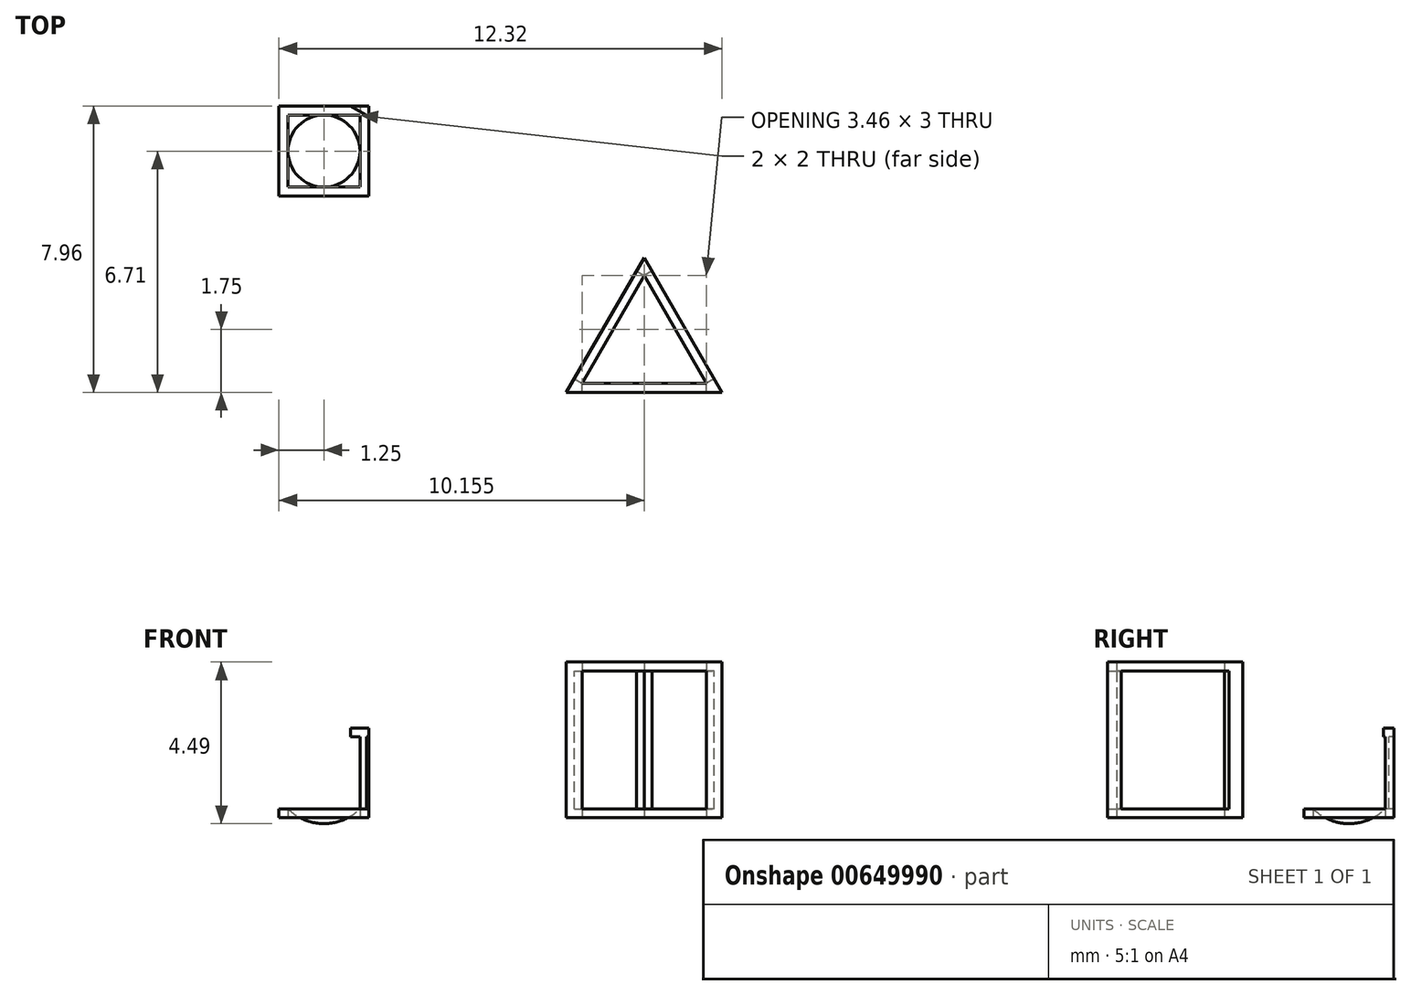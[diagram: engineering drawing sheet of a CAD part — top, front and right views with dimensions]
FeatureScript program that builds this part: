
annotation { "Feature Type Name" : "Feature", "Feature Type Description" : "" }
export const myFeature = defineFeature(function(context is Context, id is Id, definition is map)
    precondition{}
    {
        {
            var Q0;
            Q0=qCreatedBy(makeId("Top.planeOp"),FACE);
            var sketch = newSketch(context, id + "F0", { "sketchPlane" : qUnion([Q0])});
            skLineSegment(sketch, "E0.bottom", {"start": v(1, -1) * mm, "end": v(-1, -1) * mm});
            skLineSegment(sketch, "E0.top", {"start": v(1, 1) * mm, "end": v(-1, 1) * mm});
            skLineSegment(sketch, "E0.left", {"start": v(1, -1) * mm, "end": v(1, 1) * mm});
            skLineSegment(sketch, "E0.right", {"start": v(-1, -1) * mm, "end": v(-1, 1) * mm});
            skPoint(sketch, "E0.middle", {"position": v(0, 0) * mm});
            skLineSegment(sketch, "E1.bottom", {"start": v(1.25, -1.25) * mm, "end": v(-1.25, -1.25) * mm});
            skLineSegment(sketch, "E1.top", {"start": v(1.25, 1.25) * mm, "end": v(-1.25, 1.25) * mm});
            skLineSegment(sketch, "E1.left", {"start": v(1.25, -1.25) * mm, "end": v(1.25, 1.25) * mm});
            skLineSegment(sketch, "E1.right", {"start": v(-1.25, -1.25) * mm, "end": v(-1.25, 1.25) * mm});
            skSolve(sketch);
        }
        {
            var Q0;
            Q0 = qSketchRegion(id + "F0", true);
            extrude(context, id + "F1", {"entities" : qUnion([Q0]), "depth" : 2.5 * mm, "offsetDistance" : 25 * mm});
        }
        {
            var Q0;
            Q0=makeQuery(id+"F1.opExtrude","SWEPT_FACE",FACE,{"disambiguationData":[OSD([sQuery(id+"F0.wireOp",EDGE,"E1.bottom")])]});
            var sketch = newSketch(context, id + "F2", { "sketchPlane" : qUnion([Q0])});
            skLineSegment(sketch, "E2.bottom", {"start": v(1, 0.25) * mm, "end": v(-1, 0.25) * mm});
            skLineSegment(sketch, "E2.top", {"start": v(1, 2.25) * mm, "end": v(-1, 2.25) * mm});
            skLineSegment(sketch, "E2.left", {"start": v(1, 0.25) * mm, "end": v(1, 2.25) * mm});
            skLineSegment(sketch, "E2.right", {"start": v(-1, 0.25) * mm, "end": v(-1, 2.25) * mm});
            skPoint(sketch, "E2.middle", {"position": v(0, 1.25) * mm});
            skSolve(sketch);
        }
        {
            var Q0;
            Q0 = qSketchRegion(id + "F2", true);
            extrude(context, id + "F3", {"entities" : qUnion([Q0]), "operationType" : NewBodyOperationType.REMOVE, "oppositeDirection" : true, "depth" : 25 * mm, "offsetDistance" : 25 * mm});
        }
        {
            var Q0;
            Q0=makeQuery(id+"F1.opExtrude","SWEPT_FACE",FACE,{"disambiguationData":[OSD([sQuery(id+"F0.wireOp",EDGE,"E1.left")])]});
            var sketch = newSketch(context, id + "F4", { "sketchPlane" : qUnion([Q0])});
            skLineSegment(sketch, "E3.bottom", {"start": v(1, 0.25) * mm, "end": v(-1, 0.25) * mm});
            skLineSegment(sketch, "E3.top", {"start": v(1, 2.25) * mm, "end": v(-1, 2.25) * mm});
            skLineSegment(sketch, "E3.left", {"start": v(1, 0.25) * mm, "end": v(1, 2.25) * mm});
            skLineSegment(sketch, "E3.right", {"start": v(-1, 0.25) * mm, "end": v(-1, 2.25) * mm});
            skPoint(sketch, "E3.middle", {"position": v(0, 1.25) * mm});
            skPoint(sketch, "E3.middle.positionSnap0", {"position": v(0, 2.5) * mm});
            skPoint(sketch, "E3.centerSnap0", {"position": v(0, 2.5) * mm});
            skSolve(sketch);
        }
        {
            var Q0;
            Q0 = qSketchRegion(id + "F4", true);
            extrude(context, id + "F5", {"entities" : qUnion([Q0]), "operationType" : NewBodyOperationType.REMOVE, "oppositeDirection" : true, "depth" : 25 * mm, "offsetDistance" : 25 * mm});
        }
        {
            var Q0;
            Q0=qCreatedBy(makeId("Top.planeOp"),FACE);
            var sketch = newSketch(context, id + "F6", { "sketchPlane" : qUnion([Q0])});
            skCircle(sketch, "E4.cCircle", {"center": v(8.9, -5.46) * mm, "radius": 1 * mm, "construction": true});
            skLineSegment(sketch, "E4.0", {"start": v(10.64, -6.46) * mm, "end": v(7.17, -6.46) * mm});
            skLineSegment(sketch, "E4.1", {"start": v(7.17, -6.46) * mm, "end": v(8.9, -3.46) * mm});
            skLineSegment(sketch, "E4.2", {"start": v(8.9, -3.46) * mm, "end": v(10.64, -6.46) * mm});
            skPoint(sketch, "E4.0.midPoint", {"position": v(8.9, -6.46) * mm});
            skLineSegment(sketch, "E5.0", {"start": v(6.74, -6.71) * mm, "end": v(8.9, -2.96) * mm});
            skLineSegment(sketch, "E5.1", {"start": v(11.07, -6.71) * mm, "end": v(6.74, -6.71) * mm});
            skLineSegment(sketch, "E5.2", {"start": v(8.9, -2.96) * mm, "end": v(11.07, -6.71) * mm});
            skSolve(sketch);
        }
        {
            var Q0;
            Q0=makeQuery(id+"F6.imprint","IMPRINT",FACE,{"disambiguationData":[TD([[makeQuery(id+"F6.imprint","IMPRINT",EDGE,{"derivedFrom":sQuery(id+"F6.wireOp",EDGE,"E4.0")}),1.0]])]});
            extrude(context, id + "F7", {"entities" : qUnion([Q0]), "depth" : 4.33 * mm, "offsetDistance" : 25 * mm});
        }
        {
            var Q0;
            Q0=qCreatedBy(makeId("Right.planeOp"),FACE);
            var sketch = newSketch(context, id + "F8", { "sketchPlane" : qUnion([Q0])});
            skLineSegment(sketch, "E6", {"start": v(0, -0.4) * mm, "end": v(0, 2.9) * mm});
            skCircle(sketch, "E7", {"center": v(0, 1.25) * mm, "radius": 1 * mm});
            skSolve(sketch);
        }
        {
            var Q0;
            {var subQ0=sQuery(id+"F8.wireOp",EDGE,"E7");var subQ1=sQuery(id+"F8.wireOp",EDGE,"E6");var subQ2=makeQuery(id+"F8.imprint","INTERSECT",VERTEX,{"disambiguationData":[OD(0.0)],"derivedFrom":[subQ1,subQ0]});Q0=makeQuery(id+"F8.imprint","IMPRINT",FACE,{"disambiguationData":[TD([[makeQuery(id+"F8.imprint","IMPRINT",EDGE,{"disambiguationData":[TD([[subQ2,-1.0]])],"derivedFrom":subQ1}),-1.0]])]});}
            var Q1;
            Q1=sQuery(id+"F8.wireOp",EDGE,"E6");
            revolve(context, id + "F9", {"entities" : qUnion([Q0]), "axis" : qUnion([Q1]), "revolveType" : RevolveType.FULL});
        }
        {
            var Q0;
            Q0=qCreatedBy(makeId("Right.planeOp"),FACE);
            var sketch = newSketch(context, id + "F10", { "sketchPlane" : qUnion([Q0])});
            skLineSegment(sketch, "E8", {"start": v(0, -0.62) * mm, "end": v(0, 3.12) * mm});
            skCircle(sketch, "E9", {"center": v(0, 1.25) * mm, "radius": 1.41 * mm});
            skSolve(sketch);
        }
        {
            var Q0;
            {var subQ0=sQuery(id+"F10.wireOp",EDGE,"E9");var subQ1=sQuery(id+"F10.wireOp",EDGE,"E8");var subQ2=makeQuery(id+"F10.imprint","INTERSECT",VERTEX,{"disambiguationData":[OD(0.0)],"derivedFrom":[subQ1,subQ0]});Q0=makeQuery(id+"F10.imprint","IMPRINT",FACE,{"disambiguationData":[TD([[makeQuery(id+"F10.imprint","IMPRINT",EDGE,{"disambiguationData":[TD([[subQ2,-1.0]])],"derivedFrom":subQ1}),-1.0]])]});}
            var Q1;
            Q1=sQuery(id+"F10.wireOp",EDGE,"E8");
            revolve(context, id + "F11", {"operationType" : NewBodyOperationType.ADD, "entities" : qUnion([Q0]), "axis" : qUnion([Q1]), "revolveType" : RevolveType.FULL});
        }
        {
            var Q0;
            Q0=makeQuery(id+"F7.opExtrude","SWEPT_FACE",FACE,{"disambiguationData":[OSD([sQuery(id+"F6.wireOp",EDGE,"E4.0")])]});
            var sketch = newSketch(context, id + "F12", { "sketchPlane" : qUnion([Q0])});
            skLineSegment(sketch, "E10.bottom", {"start": v(-7.17, 4.08) * mm, "end": v(-10.64, 4.08) * mm});
            skLineSegment(sketch, "E10.top", {"start": v(-7.17, 0.25) * mm, "end": v(-10.64, 0.25) * mm});
            skLineSegment(sketch, "E10.left", {"start": v(-7.17, 4.08) * mm, "end": v(-7.17, 0.25) * mm});
            skLineSegment(sketch, "E10.right", {"start": v(-10.64, 4.08) * mm, "end": v(-10.64, 0.25) * mm});
            skSolve(sketch);
        }
        {
            var Q0;
            Q0=makeQuery(id+"F12.imprint","IMPRINT",FACE,{"disambiguationData":[TD([[makeQuery(id+"F12.imprint","IMPRINT",EDGE,{"derivedFrom":sQuery(id+"F12.wireOp",EDGE,"E10.bottom")}),1.0]])]});
            extrude(context, id + "F13", {"entities" : qUnion([Q0]), "operationType" : NewBodyOperationType.REMOVE, "oppositeDirection" : true, "depth" : 25 * mm, "offsetDistance" : 25 * mm});
        }
        {
            var Q0;
            Q0=makeQuery(id+"F7.opExtrude","SWEPT_FACE",FACE,{"disambiguationData":[OSD([sQuery(id+"F6.wireOp",EDGE,"E4.2")])]});
            var sketch = newSketch(context, id + "F14", { "sketchPlane" : qUnion([Q0])});
            skLineSegment(sketch, "E11.bottom", {"start": v(10.91, 0.25) * mm, "end": v(7.45, 0.25) * mm});
            skLineSegment(sketch, "E11.top", {"start": v(10.91, 4.08) * mm, "end": v(7.45, 4.08) * mm});
            skLineSegment(sketch, "E11.left", {"start": v(10.91, 0.25) * mm, "end": v(10.91, 4.08) * mm});
            skLineSegment(sketch, "E11.right", {"start": v(7.45, 0.25) * mm, "end": v(7.45, 4.08) * mm});
            skSolve(sketch);
        }
        {
            var Q0;
            Q0 = qSketchRegion(id + "F14", true);
            extrude(context, id + "F15", {"entities" : qUnion([Q0]), "operationType" : NewBodyOperationType.REMOVE, "oppositeDirection" : true, "depth" : 25 * mm, "offsetDistance" : 25 * mm});
        }
        {
            var Q0;
            Q0=makeQuery(id+"F7.opExtrude","SWEPT_FACE",FACE,{"disambiguationData":[OSD([sQuery(id+"F6.wireOp",EDGE,"E4.1")])]});
            var sketch = newSketch(context, id + "F16", { "sketchPlane" : qUnion([Q0])});
            skLineSegment(sketch, "E12.bottom", {"start": v(1.46, 0.25) * mm, "end": v(-2, 0.25) * mm});
            skLineSegment(sketch, "E12.top", {"start": v(1.46, 4.08) * mm, "end": v(-2, 4.08) * mm});
            skLineSegment(sketch, "E12.left", {"start": v(1.46, 0.25) * mm, "end": v(1.46, 4.08) * mm});
            skLineSegment(sketch, "E12.right", {"start": v(-2, 0.25) * mm, "end": v(-2, 4.08) * mm});
            skSolve(sketch);
        }
        {
            var Q0;
            Q0 = qSketchRegion(id + "F16", true);
            extrude(context, id + "F17", {"entities" : qUnion([Q0]), "operationType" : NewBodyOperationType.REMOVE, "oppositeDirection" : true, "depth" : 25 * mm, "offsetDistance" : 25 * mm});
        }
    });
